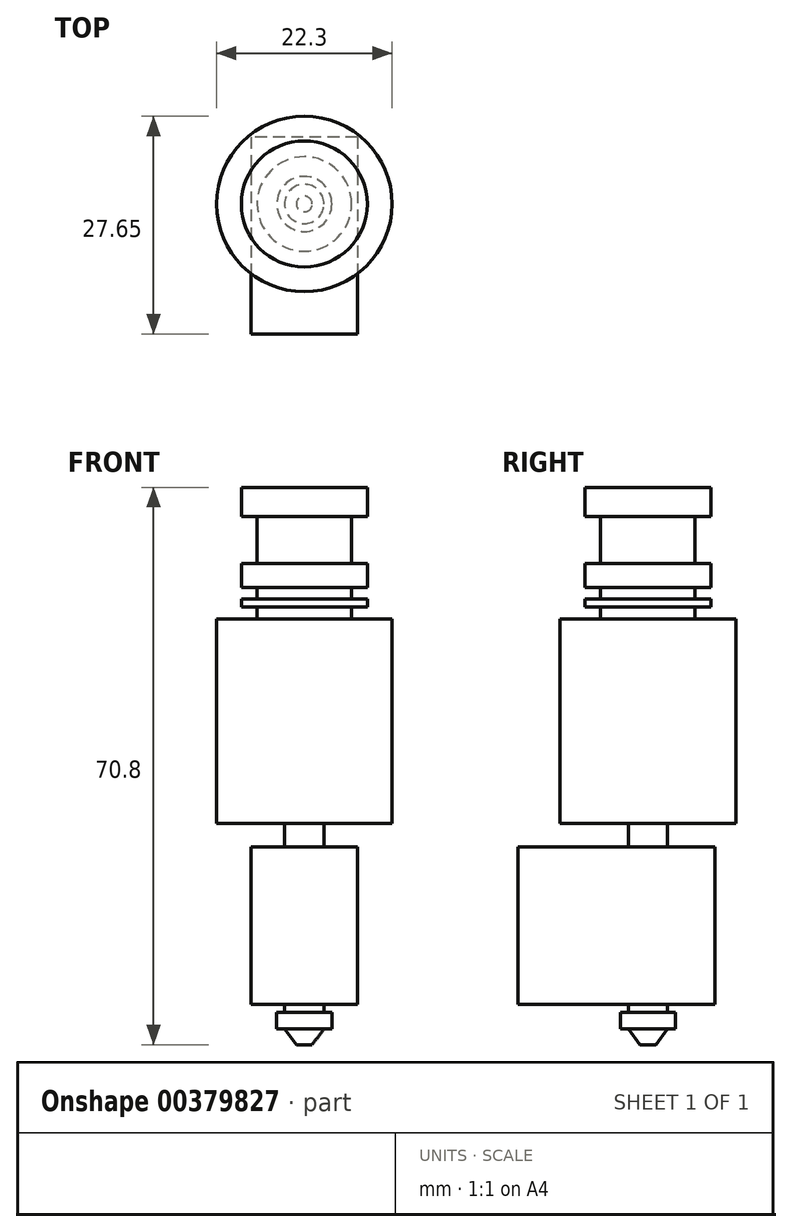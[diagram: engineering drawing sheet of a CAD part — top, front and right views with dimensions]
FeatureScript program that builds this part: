
annotation { "Feature Type Name" : "Feature", "Feature Type Description" : "" }
export const myFeature = defineFeature(function(context is Context, id is Id, definition is map)
    precondition{}
    {
        {
            var Q0;
            Q0=qCreatedBy(makeId("Front.planeOp"),FACE);
            var sketch = newSketch(context, id + "F0", { "sketchPlane" : qUnion([Q0])});
            skLineSegment(sketch, "E0.bottom", {"start": v(0, 0) * mm, "end": v(11.15, 0) * mm});
            skLineSegment(sketch, "E0.top", {"start": v(0, 42.7) * mm, "end": v(8, 42.7) * mm});
            skLineSegment(sketch, "E0.left", {"start": v(0, 0) * mm, "end": v(0, 42.7) * mm});
            skLineSegment(sketch, "E0.right", {"start": v(11.15, 0) * mm, "end": v(11.15, 26) * mm});
            skLineSegment(sketch, "E1", {"start": v(8, 42.7) * mm, "end": v(8, 39) * mm});
            skLineSegment(sketch, "E2", {"start": v(8, 39) * mm, "end": v(6, 39) * mm});
            skLineSegment(sketch, "E3", {"start": v(6, 39) * mm, "end": v(6, 33) * mm});
            skLineSegment(sketch, "E4", {"start": v(6, 33) * mm, "end": v(8, 33) * mm});
            skLineSegment(sketch, "E5", {"start": v(8, 33) * mm, "end": v(8, 30) * mm});
            skPoint(sketch, "E5.endSnap0", {"position": v(8, 40.85) * mm});
            skLineSegment(sketch, "E6", {"start": v(8, 30) * mm, "end": v(6, 30) * mm});
            skLineSegment(sketch, "E7", {"start": v(6, 30) * mm, "end": v(6, 28.5) * mm});
            skLineSegment(sketch, "E8", {"start": v(6, 28.5) * mm, "end": v(8, 28.5) * mm});
            skLineSegment(sketch, "E9", {"start": v(8, 28.5) * mm, "end": v(8, 27.5) * mm});
            skLineSegment(sketch, "E10", {"start": v(8, 27.5) * mm, "end": v(6, 27.5) * mm});
            skLineSegment(sketch, "E11", {"start": v(6, 27.5) * mm, "end": v(6, 26) * mm});
            skLineSegment(sketch, "E12", {"start": v(6, 26) * mm, "end": v(11.15, 26) * mm});
            skSolve(sketch);
        }
        {
            var Q0;
            Q0=makeQuery(id+"F0.imprint","IMPRINT",FACE,{"disambiguationData":[TD([[makeQuery(id+"F0.imprint","IMPRINT",EDGE,{"derivedFrom":sQuery(id+"F0.wireOp",EDGE,"E0.bottom")}),1.0]])]});
            var Q1;
            Q1=sQuery(id+"F0.wireOp",EDGE,"E0.left");
            revolve(context, id + "F1", {"entities" : qUnion([Q0]), "axis" : qUnion([Q1]), "revolveType" : RevolveType.FULL});
        }
        {
            var Q0;
            Q0=makeQuery(id+"F1.opRevolve","SWEPT_FACE",FACE,{"disambiguationData":[OSD([sQuery(id+"F0.wireOp",EDGE,"E0.bottom")])]});
            var sketch = newSketch(context, id + "F2", { "sketchPlane" : qUnion([Q0])});
            skCircle(sketch, "E13", {"center": v(0, 0) * mm, "radius": 2.5 * mm});
            skSolve(sketch);
        }
        {
            var Q0;
            Q0=qSketchRegion(id+"F2",true);
            extrude(context, id + "F3", {"entities" : qUnion([Q0]), "operationType" : NewBodyOperationType.ADD, "depth" : 3 * mm});
        }
        {
            var Q0;
            Q0=makeQuery(id+"F3.opExtrude","CAP_FACE",FACE,{"disambiguationData":[OSD([sQuery(id+"F2.wireOp",EDGE,"E13")])],"isStart":false});
            var sketch = newSketch(context, id + "F4", { "sketchPlane" : qUnion([Q0])});
            skLineSegment(sketch, "E14.bottom", {"start": v(6.75, -8.5) * mm, "end": v(-6.75, -8.5) * mm});
            skLineSegment(sketch, "E14.top", {"start": v(6.75, 16.5) * mm, "end": v(-6.75, 16.5) * mm});
            skLineSegment(sketch, "E14.left", {"start": v(6.75, -8.5) * mm, "end": v(6.75, 16.5) * mm});
            skLineSegment(sketch, "E14.right", {"start": v(-6.75, -8.5) * mm, "end": v(-6.75, 16.5) * mm});
            skPoint(sketch, "E14.middle", {"position": v(0, 4) * mm});
            skSolve(sketch);
        }
        {
            var Q0;
            Q0=qSketchRegion(id+"F4",true);
            extrude(context, id + "F5", {"entities" : qUnion([Q0]), "operationType" : NewBodyOperationType.ADD, "depth" : 20 * mm});
        }
        {
            var Q0;
            Q0=qCreatedBy(makeId("Front.planeOp"),FACE);
            var sketch = newSketch(context, id + "F6", { "sketchPlane" : qUnion([Q0])});
            skLineSegment(sketch, "E15.0.0", {"start": v(-6.75, -3) * mm, "end": v(6.75, -3) * mm, "construction": true});
            skLineSegment(sketch, "E15.0.1", {"start": v(6.75, -3) * mm, "end": v(6.75, -23) * mm, "construction": true});
            skLineSegment(sketch, "E15.0.2", {"start": v(6.75, -23) * mm, "end": v(-6.75, -23) * mm, "construction": true});
            skLineSegment(sketch, "E15.0.3", {"start": v(-6.75, -23) * mm, "end": v(-6.75, -3) * mm, "construction": true});
            skLineSegment(sketch, "E16", {"start": v(0, -23) * mm, "end": v(0, -28.1) * mm});
            skLineSegment(sketch, "E17", {"start": v(0, -28.1) * mm, "end": v(-1, -28.1) * mm});
            skLineSegment(sketch, "E18", {"start": v(-1, -28.1) * mm, "end": v(-2.5, -26.1) * mm});
            skLineSegment(sketch, "E19", {"start": v(-2.5, -26.1) * mm, "end": v(-3.5, -26.1) * mm});
            skLineSegment(sketch, "E20", {"start": v(-3.5, -26.1) * mm, "end": v(-3.5, -24) * mm});
            skLineSegment(sketch, "E21", {"start": v(-3.5, -24) * mm, "end": v(-2.5, -24) * mm});
            skLineSegment(sketch, "E22", {"start": v(-2.5, -24) * mm, "end": v(-2.5, -23) * mm});
            skLineSegment(sketch, "E23", {"start": v(-2.5, -23) * mm, "end": v(0, -23) * mm});
            skLineSegment(sketch, "E24", {"start": v(-11.15, 0) * mm, "end": v(-11.15, 26) * mm, "construction": true});
            skLineSegment(sketch, "E25", {"start": v(11.15, 26) * mm, "end": v(11.15, 0) * mm, "construction": true});
            skSolve(sketch);
        }
        {
            var Q0;
            Q0=qSketchRegion(id+"F6",true);
            var Q1;
            Q1=sQuery(id+"F6.wireOp",EDGE,"E16");
            revolve(context, id + "F7", {"operationType" : NewBodyOperationType.ADD, "entities" : qUnion([Q0]), "axis" : qUnion([Q1]), "revolveType" : RevolveType.FULL});
        }
    });
